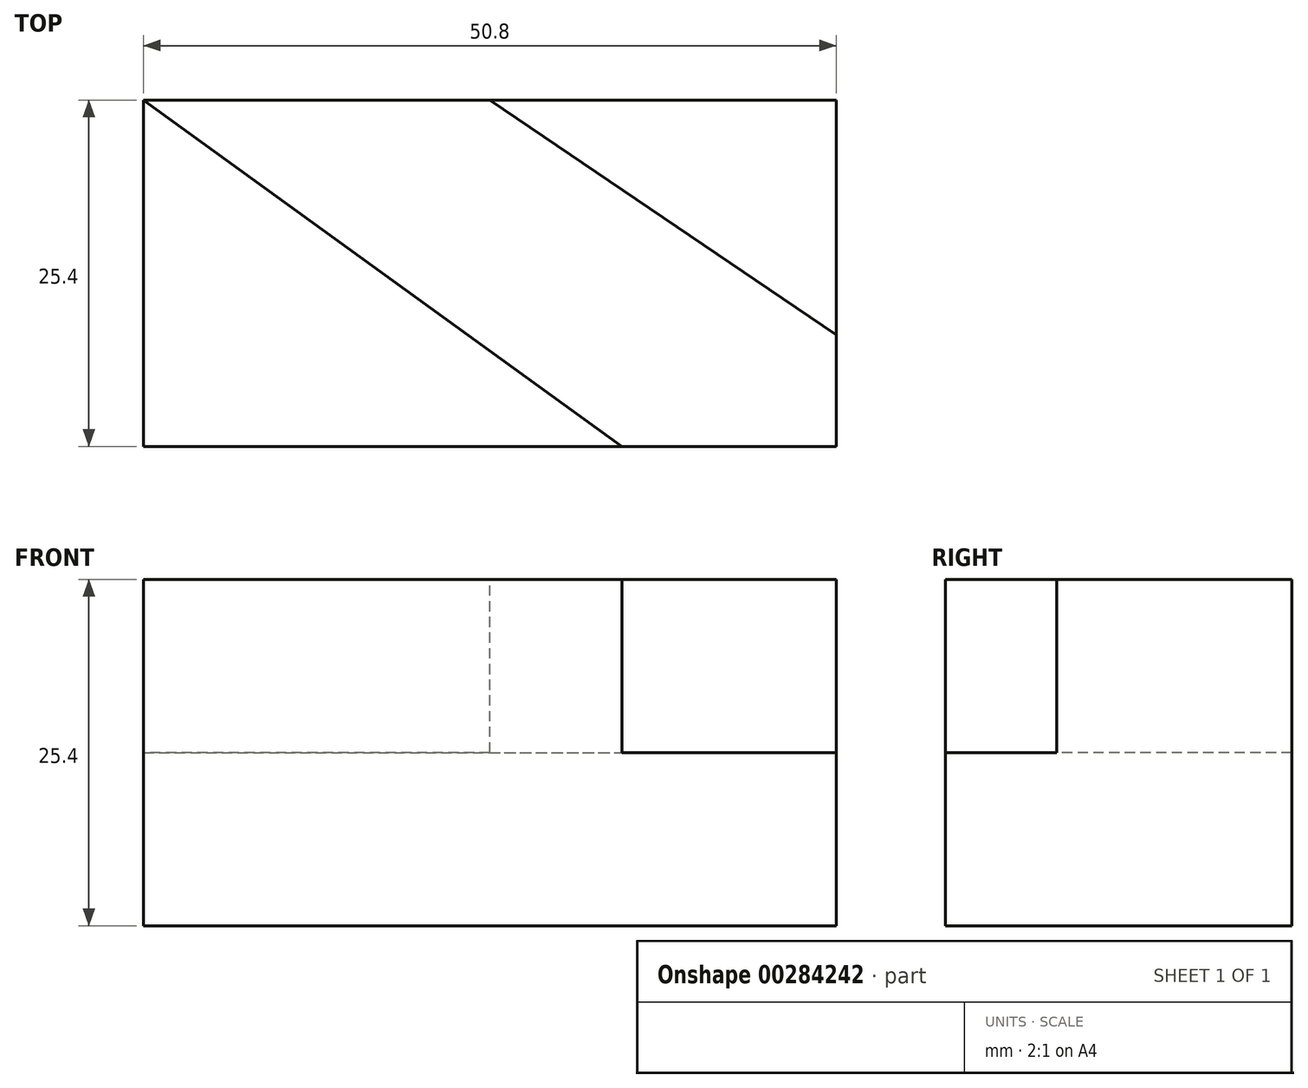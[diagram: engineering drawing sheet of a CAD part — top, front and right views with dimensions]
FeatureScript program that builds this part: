
annotation { "Feature Type Name" : "Feature", "Feature Type Description" : "" }
export const myFeature = defineFeature(function(context is Context, id is Id, definition is map)
    precondition{}
    {
        {
            var Q0;
            Q0=qCreatedBy(makeId("Front.planeOp"),FACE);
            var sketch = newSketch(context, id + "F0", { "sketchPlane" : qUnion([Q0])});
            skLineSegment(sketch, "E0", {"start": v(0, 0) * mm, "end": v(50.8, 0) * mm});
            skLineSegment(sketch, "E1", {"start": v(50.8, 0) * mm, "end": v(50.8, 25.4) * mm});
            skLineSegment(sketch, "E2", {"start": v(50.8, 25.4) * mm, "end": v(0, 25.4) * mm});
            skLineSegment(sketch, "E3", {"start": v(0, 25.4) * mm, "end": v(0, 0) * mm});
            skLineSegment(sketch, "E4", {"start": v(38.1, 25.4) * mm, "end": v(38.1, 12.7) * mm});
            skLineSegment(sketch, "E5", {"start": v(38.1, 12.7) * mm, "end": v(50.8, 12.7) * mm});
            skSolve(sketch);
        }
        {
            var Q0;
            Q0 = qSketchRegion(id + "F0", true);
            extrude(context, id + "F1", {"entities" : qUnion([Q0]), "depth" : 25.4 * mm});
        }
        {
            var Q0;
            Q0=makeQuery(id+"F1.opExtrude","SWEPT_FACE",FACE,{"disambiguationData":[OSD([sQuery(id+"F0.wireOp",EDGE,"E2")])]});
            var sketch = newSketch(context, id + "F2", { "sketchPlane" : qUnion([Q0])});
            skLineSegment(sketch, "E6", {"start": v(0, 0) * mm, "end": v(35.07, -25.4) * mm});
            skLineSegment(sketch, "E7", {"start": v(25.4, 0) * mm, "end": v(50.8, -17.23) * mm});
            skSolve(sketch);
        }
        {
            var Q0;
            Q0 = qSketchRegion(id + "F2", true);
            var Q1;
            {var subQ5=sQuery(id+"F2.wireOp",EDGE,"E6");Q1=makeQuery(id+"F2.imprint","IMPRINT",FACE,{"disambiguationData":[TD([[makeQuery(id+"F2.imprint","IMPRINT",EDGE,{"derivedFrom":subQ5}),1.0]])]});}
            extrude(context, id + "F3", {"entities" : qUnion([Q0, Q1]), "operationType" : NewBodyOperationType.REMOVE, "endBound" : BoundingType.SYMMETRIC, "oppositeDirection" : true, "depth" : 25.4 * mm});
        }
    });
